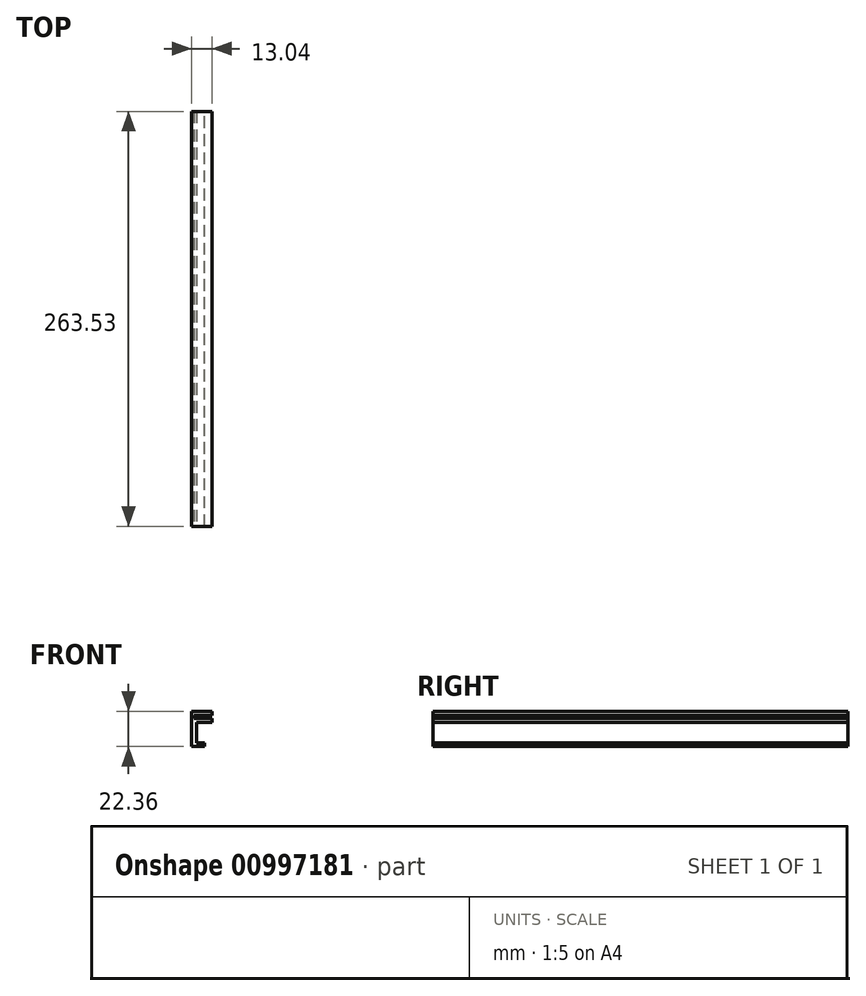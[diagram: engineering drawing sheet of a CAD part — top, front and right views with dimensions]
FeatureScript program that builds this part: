
annotation { "Feature Type Name" : "Feature", "Feature Type Description" : "" }
export const myFeature = defineFeature(function(context is Context, id is Id, definition is map)
    precondition{}
    {
        {
            var Q0;
            Q0=qCreatedBy(makeId("Front.planeOp"),FACE);
            var sketch = newSketch(context, id + "F0", { "sketchPlane" : qUnion([Q0])});
            skLineSegment(sketch, "E0.bottom", {"start": v(-6.52, 11.18) * mm, "end": v(6.52, 11.18) * mm});
            skLineSegment(sketch, "E0.top", {"start": v(-6.52, -11.18) * mm, "end": v(6.52, -11.18) * mm});
            skLineSegment(sketch, "E0.left", {"start": v(-6.52, 11.18) * mm, "end": v(-6.52, -11.18) * mm});
            skLineSegment(sketch, "E0.right", {"start": v(6.52, 11.18) * mm, "end": v(6.52, -11.18) * mm});
            skPoint(sketch, "E0.middle", {"position": v(0, 0) * mm});
            skSolve(sketch);
        }
        {
            var Q0;
            Q0 = qSketchRegion(id + "F0", true);
            extrude(context, id + "F1", {"entities" : qUnion([Q0]), "depth" : 263.52 * mm, "offsetDistance" : 25.4 * mm});
        }
        {
            var Q0;
            Q0=makeQuery(id+"F1.opExtrude","CAP_FACE",FACE,{"disambiguationData":[OSD([sQuery(id+"F0.wireOp",EDGE,"E0.bottom"),sQuery(id+"F0.wireOp",EDGE,"E0.top"),sQuery(id+"F0.wireOp",EDGE,"E0.left"),sQuery(id+"F0.wireOp",EDGE,"E0.right")])],"isStart":false});
            var sketch = newSketch(context, id + "F2", { "sketchPlane" : qUnion([Q0])});
            skLineSegment(sketch, "E1.bottom", {"start": v(6.52, 8.64) * mm, "end": v(-4.81, 8.64) * mm});
            skLineSegment(sketch, "E1.top", {"start": v(6.52, 6.6) * mm, "end": v(-4.81, 6.6) * mm});
            skLineSegment(sketch, "E1.left", {"start": v(6.52, 8.64) * mm, "end": v(6.52, 6.6) * mm});
            skLineSegment(sketch, "E1.right", {"start": v(-4.81, 8.64) * mm, "end": v(-4.81, 6.6) * mm});
            skSolve(sketch);
        }
        {
            var Q0;
            Q0=makeQuery(id+"F2.imprint","IMPRINT",FACE,{"disambiguationData":[TD([[makeQuery(id+"F2.imprint","IMPRINT",EDGE,{"derivedFrom":sQuery(id+"F2.wireOp",EDGE,"E1.bottom")}),1.0]])]});
            extrude(context, id + "F3", {"entities" : qUnion([Q0]), "operationType" : NewBodyOperationType.REMOVE, "endBound" : BoundingType.THROUGH_ALL, "oppositeDirection" : true, "depth" : 25.4 * mm, "offsetDistance" : 25.4 * mm});
        }
        {
            var Q0;
            Q0=makeQuery(id+"F1.opExtrude","CAP_FACE",FACE,{"disambiguationData":[OSD([sQuery(id+"F0.wireOp",EDGE,"E0.bottom"),sQuery(id+"F0.wireOp",EDGE,"E0.top"),sQuery(id+"F0.wireOp",EDGE,"E0.left"),sQuery(id+"F0.wireOp",EDGE,"E0.right")])],"isStart":false});
            var sketch = newSketch(context, id + "F4", { "sketchPlane" : qUnion([Q0])});
            skLineSegment(sketch, "E2.bottom", {"start": v(6.52, 4.06) * mm, "end": v(-3.34, 4.06) * mm});
            skLineSegment(sketch, "E2.top", {"start": v(6.52, -9.02) * mm, "end": v(-3.34, -9.02) * mm});
            skLineSegment(sketch, "E2.left", {"start": v(6.52, 4.06) * mm, "end": v(6.52, -9.02) * mm});
            skLineSegment(sketch, "E2.right", {"start": v(-3.34, 4.06) * mm, "end": v(-3.34, -9.02) * mm});
            skSolve(sketch);
        }
        {
            var Q0;
            Q0=makeQuery(id+"F4.imprint","IMPRINT",FACE,{"disambiguationData":[TD([[makeQuery(id+"F4.imprint","IMPRINT",EDGE,{"derivedFrom":sQuery(id+"F4.wireOp",EDGE,"E2.bottom")}),1.0]])]});
            extrude(context, id + "F5", {"entities" : qUnion([Q0]), "operationType" : NewBodyOperationType.REMOVE, "endBound" : BoundingType.THROUGH_ALL, "oppositeDirection" : true, "depth" : 25.4 * mm, "offsetDistance" : 25.4 * mm});
        }
        {
            var Q0;
            {var subQ0=sQuery(id+"F0.wireOp",EDGE,"E0.right");var subQ2=sQuery(id+"F0.wireOp",EDGE,"E0.top");var subQ6=makeQuery(id+"F1.opExtrude","SWEPT_FACE",FACE,{"disambiguationData":[OSD([subQ2])]});Q0=makeQuery(id+"F5.boolean.opBoolean","SPLIT",FACE,{"disambiguationData":[TD([subQ6])],"derivedFrom":makeQuery(id+"F3.boolean.opBoolean","SPLIT",FACE,{"disambiguationData":[TD([subQ6])],"derivedFrom":makeQuery(id+"F1.opExtrude","SWEPT_FACE",FACE,{"disambiguationData":[OSD([subQ0])]})})});}
            var sketch = newSketch(context, id + "F6", { "sketchPlane" : qUnion([Q0])});
            skLineSegment(sketch, "E3.0.0", {"start": v(0, -11.18) * mm, "end": v(0, -9.02) * mm});
            skLineSegment(sketch, "E3.0.1", {"start": v(0, -9.02) * mm, "end": v(-263.53, -9.02) * mm});
            skLineSegment(sketch, "E3.0.2", {"start": v(-263.53, -9.02) * mm, "end": v(-263.53, -11.18) * mm});
            skLineSegment(sketch, "E3.0.3", {"start": v(-263.53, -11.18) * mm, "end": v(0, -11.18) * mm});
            skSolve(sketch);
        }
        {
            var Q0;
            Q0 = qSketchRegion(id + "F6", true);
            extrude(context, id + "F7", {"entities" : qUnion([Q0]), "operationType" : NewBodyOperationType.REMOVE, "oppositeDirection" : true, "depth" : 4.7 * mm, "offsetDistance" : 25.4 * mm});
        }
    });
